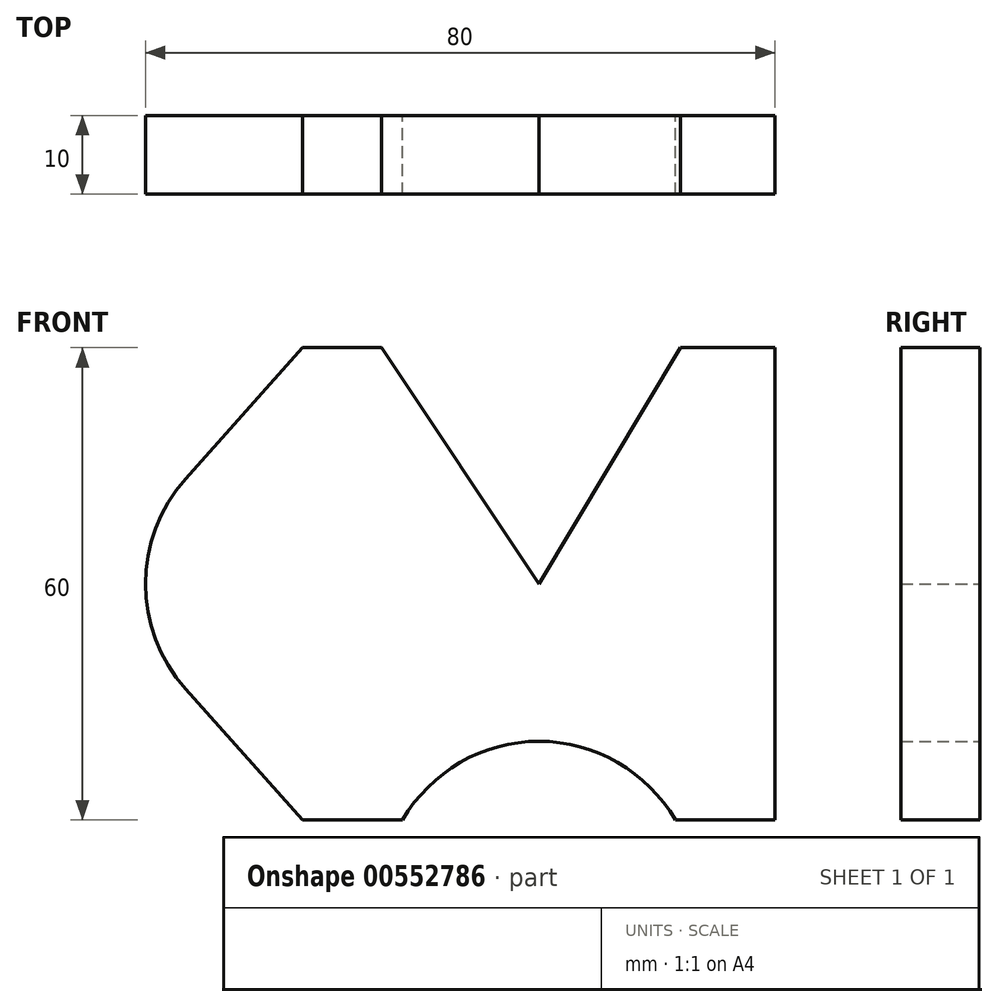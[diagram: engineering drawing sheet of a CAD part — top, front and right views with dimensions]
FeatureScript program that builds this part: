
annotation { "Feature Type Name" : "Feature", "Feature Type Description" : "" }
export const myFeature = defineFeature(function(context is Context, id is Id, definition is map)
    precondition{}
    {
        {
            var Q0;
            Q0=qCreatedBy(makeId("Front.planeOp"),FACE);
            var sketch = newSketch(context, id + "F0", { "sketchPlane" : qUnion([Q0])});
            skLineSegment(sketch, "E0", {"start": v(18, 30) * mm, "end": v(30, 30) * mm});
            skLineSegment(sketch, "E1", {"start": v(30, 30) * mm, "end": v(30, -30) * mm});
            skLineSegment(sketch, "E2", {"start": v(30, -30) * mm, "end": v(17.32, -30) * mm});
            skLineSegment(sketch, "E3", {"start": v(0, 0) * mm, "end": v(-20, 30) * mm});
            skLineSegment(sketch, "E4", {"start": v(-20, 30) * mm, "end": v(-30, 30) * mm});
            skLineSegment(sketch, "E5", {"start": v(-30, 30) * mm, "end": v(-44.9, 13.33) * mm});
            skArc(sketch, "E6", {"start": v(17.32, -30) * mm, "mid": v(0, -20) * mm, "end": v(-17.32, -30) * mm});
            skLineSegment(sketch, "E7", {"start": v(-17.32, -30) * mm, "end": v(-30, -30) * mm});
            skLineSegment(sketch, "E8", {"start": v(-30, -30) * mm, "end": v(-44.9, -13.33) * mm});
            skArc(sketch, "E9", {"start": v(-44.9, 13.33) * mm, "mid": v(-50, 0) * mm, "end": v(-44.9, -13.33) * mm});
            skLineSegment(sketch, "E10", {"start": v(-30, 30) * mm, "end": v(-30, -30) * mm, "construction": true});
            skLineSegment(sketch, "E11", {"start": v(18, 30) * mm, "end": v(0, 0) * mm});
            skSolve(sketch);
        }
        {
            var Q0;
            Q0=makeQuery(id+"F0.imprint","IMPRINT",FACE,{"disambiguationData":[TD([[makeQuery(id+"F0.imprint","IMPRINT",EDGE,{"derivedFrom":sQuery(id+"F0.wireOp",EDGE,"E0")}),-1.0]])]});
            extrude(context, id + "F1", {"entities" : qUnion([Q0]), "depth" : 10 * mm, "offsetDistance" : 25 * mm});
        }
    });
